# Revit family: BV1280
name_source: partatom
category: Plumbing Fixtures
revit_build: Autodesk Revit Structure 2013 (Build: 20120221_2030(x64)
units: mm (PartAtom-declared; Revit-internal decimal feet)

## types (10) — shared parameters
Body Material = Steel
Description = Terminal valve
Manufacturer = Mifab
Model = BV1280
URL = www.mifab.com

## per-type parameters (varying)
| type | Diameter | Flapper size | Length | Pipe size | Upper steel body |
| BV1282 | 3' - 1 1/2" | 1' - 9" | 5' - 3" | 1' - 0" | 1' - 9" |
| BV1284 | 4' - 6" | 1' - 11" | 5' - 9" | 2' - 0" | 1' - 11" |
| BV1280-18 | 13' - 1 1/2" | 5' - 4" | 16' - 0" | 9' - 0" | 5' - 4" |
| BV1283 | 4' - 0" | 1' - 10" | 5' - 6" | 1' - 6" | 1' - 10" |
| BV1285 | 5' - 9" | 2' - 0" | 6' - 0" | 2' - 6" | 2' - 0" |
| BV1286 | 5' - 9" | 2' - 0" | 6' - 0" | 3' - 0" | 2' - 0" |
| BV1288 | 6' - 9" | 2' - 3" | 6' - 9" | 4' - 0" | 2' - 3" |
| BV1280-10 | 7' - 10 1/2" | 2' - 7" | 7' - 9" | 5' - 0" | 2' - 7" |
| BV1280-12 | 8' - 9" | 2' - 11" | 8' - 9" | 6' - 0" | 2' - 11" |
| BV1280-16 | 13' - 1 1/2" | 5' - 6" | 16' - 6" | 8' - 0" | 5' - 6" |

## geometry (parser evidence)
native form markers: Blend x5, Sweep x1
no freeform markers — native parametric forms only
